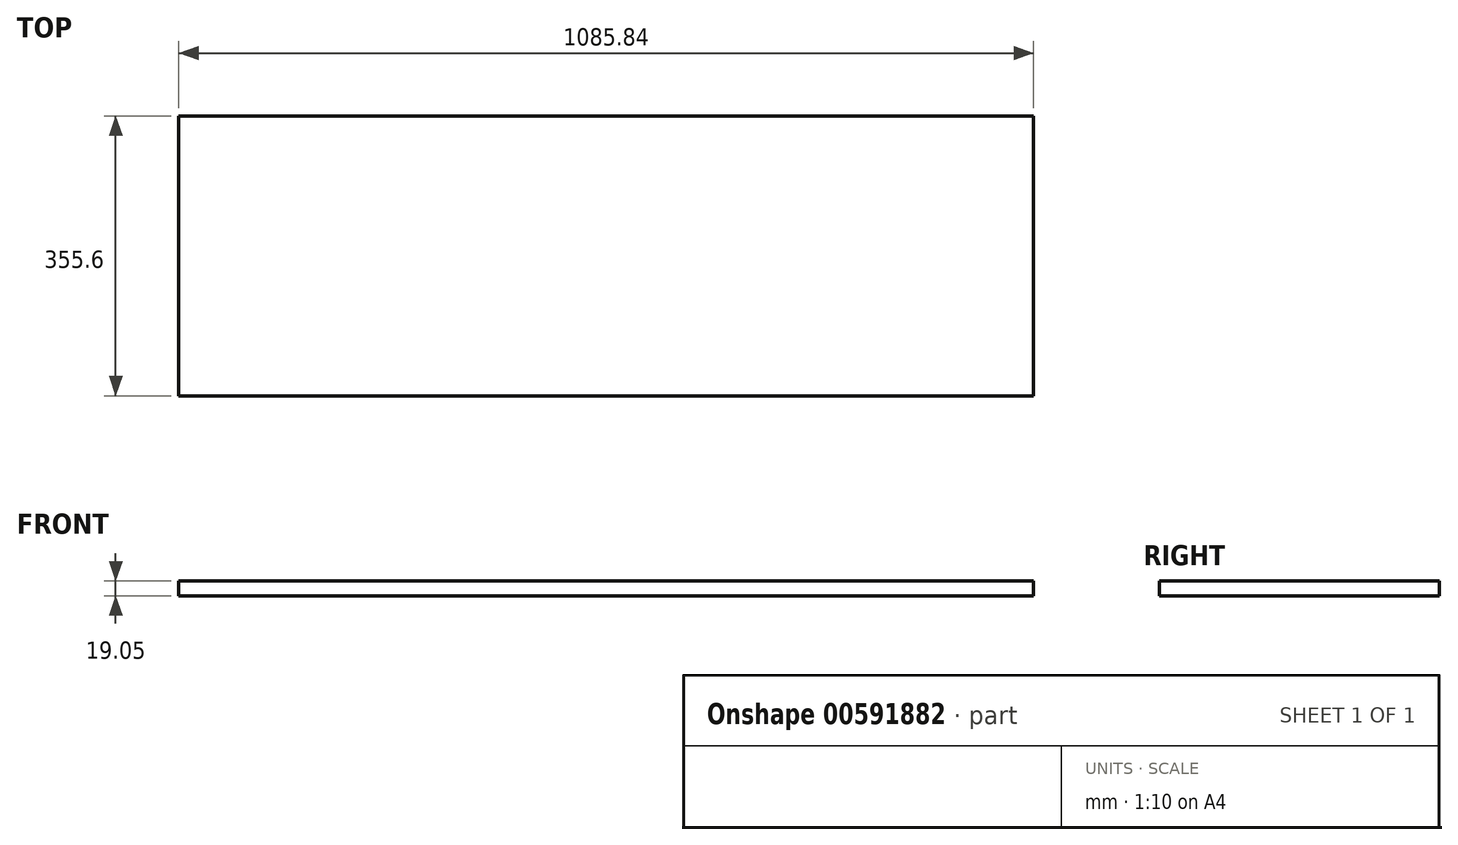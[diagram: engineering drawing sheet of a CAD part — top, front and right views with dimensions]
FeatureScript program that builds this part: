
annotation { "Feature Type Name" : "Feature", "Feature Type Description" : "" }
export const myFeature = defineFeature(function(context is Context, id is Id, definition is map)
    precondition{}
    {
        {
            var Q0;
            Q0=qCreatedBy(makeId("Top.planeOp"),FACE);
            var sketch = newSketch(context, id + "F0", { "sketchPlane" : qUnion([Q0])});
            skLineSegment(sketch, "E0.bottom", {"start": v(542.93, 177.8) * mm, "end": v(-542.93, 177.8) * mm});
            skLineSegment(sketch, "E0.top", {"start": v(542.93, -177.8) * mm, "end": v(-542.93, -177.8) * mm});
            skLineSegment(sketch, "E0.left", {"start": v(542.93, 177.8) * mm, "end": v(542.93, -177.8) * mm});
            skLineSegment(sketch, "E0.right", {"start": v(-542.93, 177.8) * mm, "end": v(-542.93, -177.8) * mm});
            skPoint(sketch, "E0.middle", {"position": v(0, 0) * mm});
            skSolve(sketch);
        }
        {
            var Q0;
            Q0=makeQuery(id+"F0.imprint","IMPRINT",FACE,{"disambiguationData":[TD([[makeQuery(id+"F0.imprint","IMPRINT",EDGE,{"derivedFrom":sQuery(id+"F0.wireOp",EDGE,"E0.bottom")}),1.0]])]});
            extrude(context, id + "F1", {"entities" : qUnion([Q0]), "depth" : 19.05 * mm, "offsetDistance" : 25.4 * mm});
        }
    });
